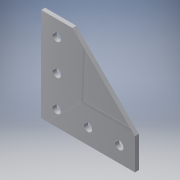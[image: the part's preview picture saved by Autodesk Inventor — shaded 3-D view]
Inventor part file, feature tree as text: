
AUTODESK INVENTOR PART (.ipt)
format: ipt  version: 2016 (Build 200138000, 138)  size: 104,960 bytes
history: native  units: in
note: dims shown in document units (in); Inventor stores cm internally (conversion verified against a paired STEP export)
features: other x3, sketch x1
ambient origin geometry x8: Origin, YZ Plane, XZ Plane, XY Plane, X Axis, Y Axis, Z Axis, Center Point
bodies: Solid1 (feature_tree)
feature tree (4):
  other  "gusset plate.ipt"
  other  "Solid1::gusset plate.ipt"
  other  "TaggingFeature1"
  sketch  "Sketch1"  dims[d0=0.3937in]
